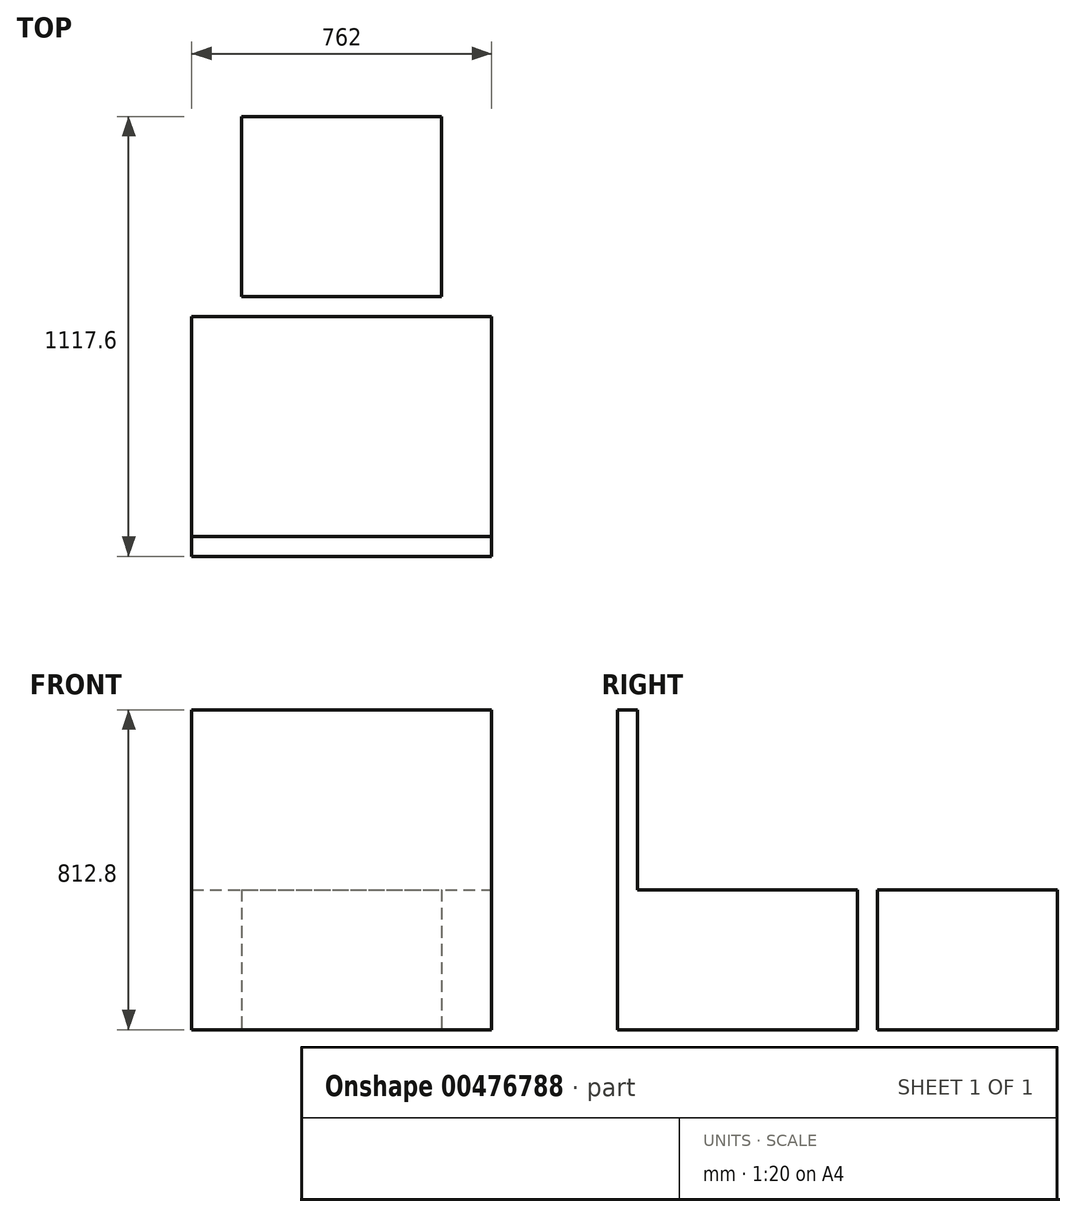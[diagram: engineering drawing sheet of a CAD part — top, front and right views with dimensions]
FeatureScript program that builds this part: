
annotation { "Feature Type Name" : "Feature", "Feature Type Description" : "" }
export const myFeature = defineFeature(function(context is Context, id is Id, definition is map)
    precondition{}
    {
        {
            var Q0;
            Q0=qCreatedBy(makeId("Top.planeOp"),FACE);
            var sketch = newSketch(context, id + "F0", { "sketchPlane" : qUnion([Q0])});
            skLineSegment(sketch, "E0.bottom", {"start": v(-381, 609.6) * mm, "end": v(381, 609.6) * mm});
            skLineSegment(sketch, "E0.top", {"start": v(-381, 0) * mm, "end": v(381, 0) * mm});
            skLineSegment(sketch, "E0.left", {"start": v(-381, 609.6) * mm, "end": v(-381, 0) * mm});
            skLineSegment(sketch, "E0.right", {"start": v(381, 609.6) * mm, "end": v(381, 0) * mm});
            skLineSegment(sketch, "E1.bottom", {"start": v(-254, 1117.6) * mm, "end": v(254, 1117.6) * mm});
            skLineSegment(sketch, "E1.top", {"start": v(-254, 660.4) * mm, "end": v(254, 660.4) * mm});
            skLineSegment(sketch, "E1.left", {"start": v(-254, 1117.6) * mm, "end": v(-254, 660.4) * mm});
            skLineSegment(sketch, "E1.right", {"start": v(254, 1117.6) * mm, "end": v(254, 660.4) * mm});
            skLineSegment(sketch, "E2", {"start": v(0, 660.4) * mm, "end": v(0, 609.6) * mm, "construction": true});
            skPoint(sketch, "E2.endSnap0", {"position": v(0, 609.6) * mm});
            skSolve(sketch);
        }
        {
            var Q0;
            Q0 = qSketchRegion(id + "F0", true);
            extrude(context, id + "F1", {"entities" : qUnion([Q0]), "depth" : 355.6 * mm, "offsetDistance" : 25.4 * mm});
        }
        {
            var Q0;
            Q0=qCreatedBy(makeId("Right.planeOp"),FACE);
            var sketch = newSketch(context, id + "F2", { "sketchPlane" : qUnion([Q0])});
            skLineSegment(sketch, "E3.bottom", {"start": v(0, 355.6) * mm, "end": v(50.8, 355.6) * mm});
            skLineSegment(sketch, "E3.top", {"start": v(0, 812.8) * mm, "end": v(50.8, 812.8) * mm});
            skLineSegment(sketch, "E3.left", {"start": v(0, 355.6) * mm, "end": v(0, 812.8) * mm});
            skLineSegment(sketch, "E3.right", {"start": v(50.8, 355.6) * mm, "end": v(50.8, 812.8) * mm});
            skSolve(sketch);
        }
        {
            var Q0;
            Q0 = qSketchRegion(id + "F2", true);
            extrude(context, id + "F3", {"entities" : qUnion([Q0]), "operationType" : NewBodyOperationType.ADD, "depth" : 381 * mm, "offsetDistance" : 25.4 * mm, "hasSecondDirection" : true, "secondDirectionOppositeDirection" : true, "secondDirectionDepth" : 381 * mm});
        }
    });
